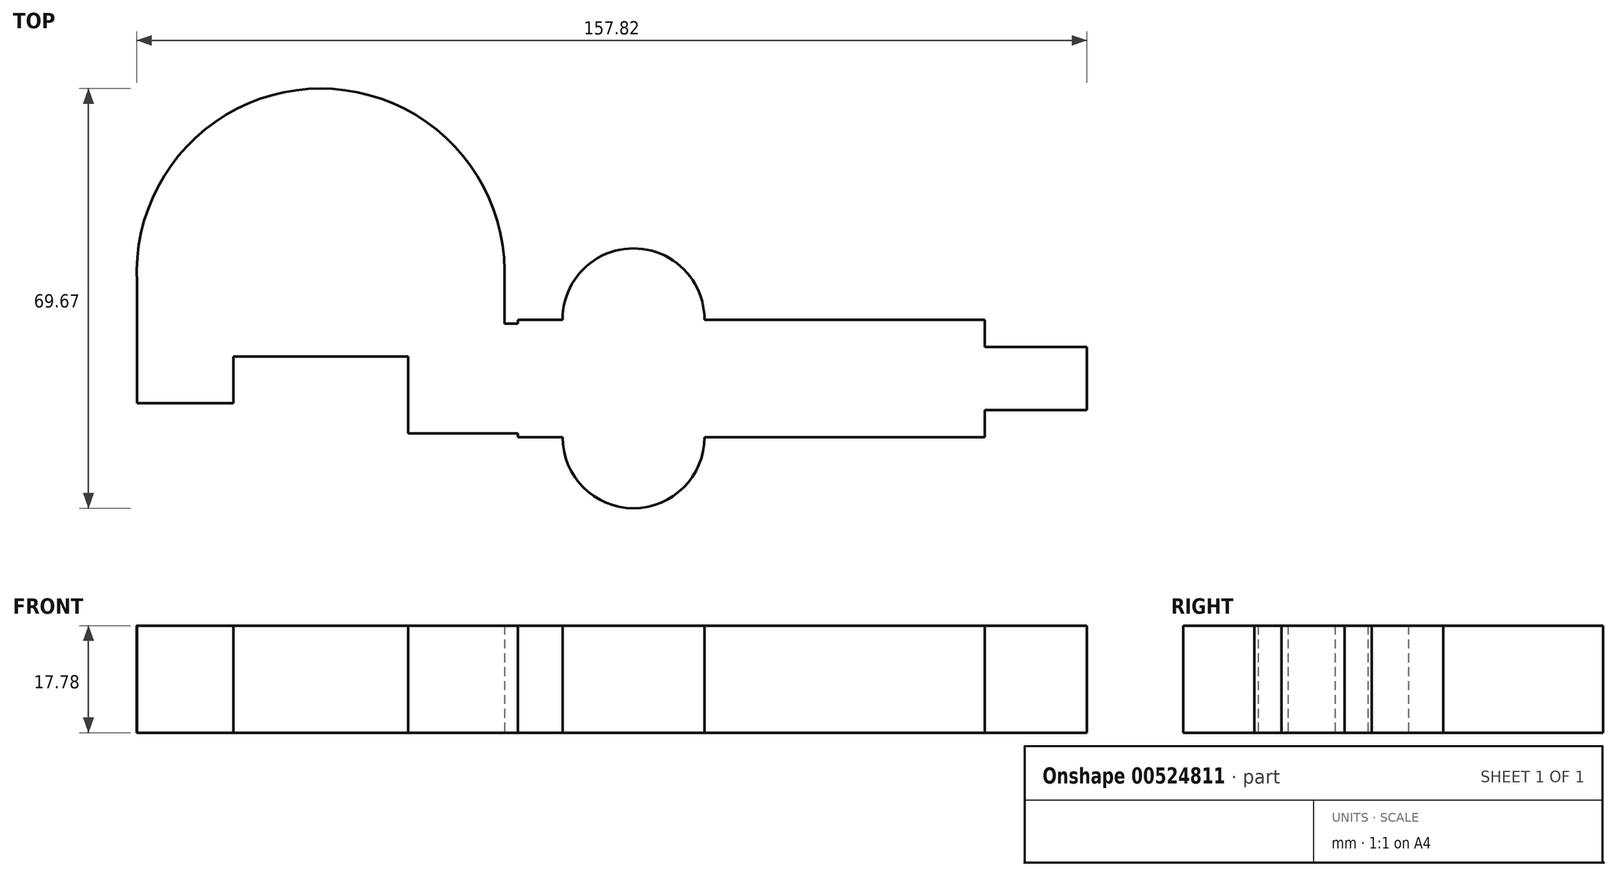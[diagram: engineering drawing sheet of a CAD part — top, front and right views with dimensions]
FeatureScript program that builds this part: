
annotation { "Feature Type Name" : "Feature", "Feature Type Description" : "" }
export const myFeature = defineFeature(function(context is Context, id is Id, definition is map)
    precondition{}
    {
        {
            var Q0;
            Q0=qCreatedBy(makeId("Top.planeOp"),FACE);
            var sketch = newSketch(context, id + "F0", { "sketchPlane" : qUnion([Q0])});
            skArc(sketch, "E0.0", {"start": v(-63.05, -48.26) * mm, "mid": v(-93.56, -15.99) * mm, "end": v(-124.07, -48.26) * mm});
            skLineSegment(sketch, "E0.1", {"start": v(-63.05, -61) * mm, "end": v(-63.05, -48.26) * mm});
            skLineSegment(sketch, "E0.2", {"start": v(-60.8, -54.99) * mm, "end": v(-79.07, -54.99) * mm});
            skLineSegment(sketch, "E0.3", {"start": v(-60.8, -73.25) * mm, "end": v(-60.8, -54.99) * mm});
            skLineSegment(sketch, "E0.6", {"start": v(16.7, -54.36) * mm, "end": v(-60.8, -54.36) * mm});
            skLineSegment(sketch, "E0.7", {"start": v(16.7, -73.88) * mm, "end": v(16.7, -54.36) * mm});
            skLineSegment(sketch, "E0.8", {"start": v(33.7, -58.86) * mm, "end": v(15.68, -58.86) * mm});
            skLineSegment(sketch, "E0.9", {"start": v(33.7, -69.38) * mm, "end": v(33.7, -58.86) * mm});
            skLineSegment(sketch, "E0.10", {"start": v(15.68, -69.38) * mm, "end": v(33.7, -69.38) * mm});
            skLineSegment(sketch, "E0.11", {"start": v(-23.93, -73.88) * mm, "end": v(16.7, -73.88) * mm});
            skLineSegment(sketch, "E0.14", {"start": v(-79.07, -73.25) * mm, "end": v(-60.8, -73.25) * mm});
            skLineSegment(sketch, "E0.15", {"start": v(-79.07, -73.25) * mm, "end": v(-79.07, -54.99) * mm});
            skLineSegment(sketch, "E0.16", {"start": v(-109.07, -67.75) * mm, "end": v(-78.05, -67.75) * mm});
            skLineSegment(sketch, "E0.17", {"start": v(-78.05, -60.5) * mm, "end": v(-109.07, -60.5) * mm});
            skLineSegment(sketch, "E0.18", {"start": v(-108.05, -68.25) * mm, "end": v(-108.05, -54.99) * mm});
            skLineSegment(sketch, "E0.19", {"start": v(-108.05, -56) * mm, "end": v(-108.05, -50.51) * mm});
            skArc(sketch, "E0.20", {"start": v(-79.07, -50.51) * mm, "mid": v(-93.56, -37) * mm, "end": v(-108.05, -50.51) * mm});
            skLineSegment(sketch, "E0.21", {"start": v(-79.07, -61) * mm, "end": v(-79.07, -50.51) * mm});
            skLineSegment(sketch, "E0.22", {"start": v(-108.05, -68.25) * mm, "end": v(-124.07, -68.25) * mm});
            skLineSegment(sketch, "E0.23", {"start": v(-124.07, -54.99) * mm, "end": v(-124.07, -68.25) * mm});
            skLineSegment(sketch, "E0.24", {"start": v(-124.07, -56) * mm, "end": v(-124.07, -48.26) * mm});
            skLineSegment(sketch, "E1", {"start": v(-60.8, -54.36) * mm, "end": v(-60.8, -54.99) * mm});
            skLineSegment(sketch, "E2", {"start": v(-60.8, -54.36) * mm, "end": v(-60.8, -73.88) * mm});
            skLineSegment(sketch, "E3", {"start": v(-60.8, -73.88) * mm, "end": v(-23.93, -73.88) * mm});
            skArc(sketch, "E4", {"start": v(-29.83, -54.36) * mm, "mid": v(-41.6, -42.52) * mm, "end": v(-53.4, -54.36) * mm});
            skArc(sketch, "E5", {"start": v(-53.4, -73.88) * mm, "mid": v(-41.6, -85.66) * mm, "end": v(-29.83, -73.88) * mm});
            skSolve(sketch);
        }
        {
            var Q0;
            {var subQ7=sQuery(id+"F0.wireOp",EDGE,"E0.0");Q0=makeQuery(id+"F0.imprint","IMPRINT",FACE,{"disambiguationData":[TD([[makeQuery(id+"F0.imprint","IMPRINT",EDGE,{"derivedFrom":subQ7}),1.0]])]});}
            var Q1;
            {var subQ5=sQuery(id+"F0.wireOp",EDGE,"E0.21");var subQ7=sQuery(id+"F0.wireOp",EDGE,"E0.15");var subQ9=makeQuery(id+"F0.imprint","INTERSECT",VERTEX,{"derivedFrom":[subQ7,subQ5]});Q1=makeQuery(id+"F0.imprint","IMPRINT",FACE,{"disambiguationData":[TD([[makeQuery(id+"F0.imprint","IMPRINT",EDGE,{"disambiguationData":[TD([[subQ9,1.0]])],"derivedFrom":subQ7}),1.0]])]});}
            var Q2;
            {var subQ1=sQuery(id+"F0.wireOp",EDGE,"E0.14");Q2=makeQuery(id+"F0.imprint","IMPRINT",FACE,{"disambiguationData":[TD([[makeQuery(id+"F0.imprint","IMPRINT",EDGE,{"derivedFrom":subQ1}),1.0]])]});}
            var Q3;
            {var subQ1=sQuery(id+"F0.wireOp",EDGE,"E0.6");Q3=makeQuery(id+"F0.imprint","IMPRINT",FACE,{"disambiguationData":[TD([[makeQuery(id+"F0.imprint","IMPRINT",EDGE,{"derivedFrom":subQ1}),1.0]])]});}
            var Q4;
            {var subQ5=sQuery(id+"F0.wireOp",EDGE,"E0.9");Q4=makeQuery(id+"F0.imprint","IMPRINT",FACE,{"disambiguationData":[TD([[makeQuery(id+"F0.imprint","IMPRINT",EDGE,{"derivedFrom":subQ5}),1.0]])]});}
            var Q5;
            {var subQ0=sQuery(id+"F0.wireOp",EDGE,"E4");Q5=makeQuery(id+"F0.imprint","IMPRINT",FACE,{"disambiguationData":[TD([[makeQuery(id+"F0.imprint","IMPRINT",EDGE,{"derivedFrom":subQ0}),1.0]])]});}
            var Q6;
            {var subQ0=sQuery(id+"F0.wireOp",EDGE,"E5");Q6=makeQuery(id+"F0.imprint","IMPRINT",FACE,{"disambiguationData":[TD([[makeQuery(id+"F0.imprint","IMPRINT",EDGE,{"derivedFrom":subQ0}),1.0]])]});}
            extrude(context, id + "F1", {"entities" : qUnion([Q0, Q1, Q2, Q3, Q4, Q5, Q6]), "depth" : 17.78 * mm, "offsetDistance" : 25.4 * mm});
        }
    });
